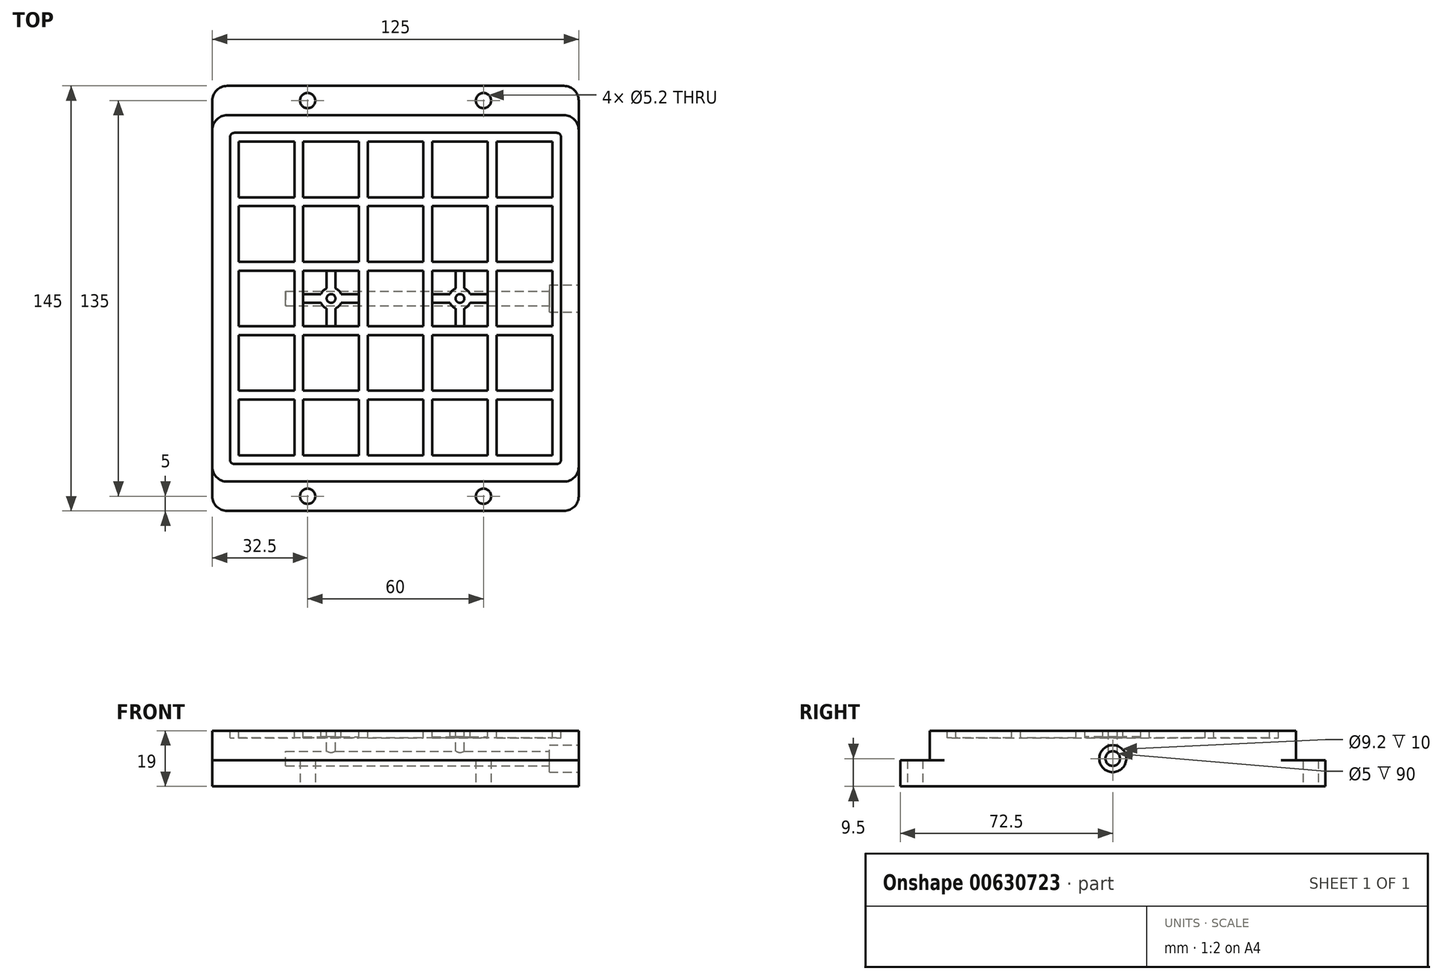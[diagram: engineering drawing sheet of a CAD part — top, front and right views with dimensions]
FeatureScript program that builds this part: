
annotation { "Feature Type Name" : "Feature", "Feature Type Description" : "" }
export const myFeature = defineFeature(function(context is Context, id is Id, definition is map)
    precondition{}
    {
        {
            var Q0;
            Q0=qCreatedBy(makeId("Top.planeOp"),FACE);
            var sketch = newSketch(context, id + "F0", { "sketchPlane" : qUnion([Q0])});
            skLineSegment(sketch, "E0.bottom", {"start": v(57.5, -72.5) * mm, "end": v(-57.5, -72.5) * mm});
            skLineSegment(sketch, "E0.top", {"start": v(57.5, 72.5) * mm, "end": v(-57.5, 72.5) * mm});
            skLineSegment(sketch, "E0.left", {"start": v(62.5, -67.5) * mm, "end": v(62.5, 67.5) * mm});
            skLineSegment(sketch, "E0.right", {"start": v(-62.5, -67.5) * mm, "end": v(-62.5, 67.5) * mm});
            skPoint(sketch, "E0.middle", {"position": v(0, 0) * mm});
            skPoint(sketch, "E1.visualSharp", {"position": v(-62.5, 72.5) * mm});
            skArc(sketch, "E1.filletArc", {"start": v(-57.5, 72.5) * mm, "mid": v(-61.04, 71.04) * mm, "end": v(-62.5, 67.5) * mm});
            skPoint(sketch, "E2.visualSharp", {"position": v(62.5, 72.5) * mm});
            skArc(sketch, "E2.filletArc", {"start": v(62.5, 67.5) * mm, "mid": v(61.04, 71.04) * mm, "end": v(57.5, 72.5) * mm});
            skPoint(sketch, "E3.visualSharp", {"position": v(62.5, -72.5) * mm});
            skArc(sketch, "E3.filletArc", {"start": v(57.5, -72.5) * mm, "mid": v(61.04, -71.04) * mm, "end": v(62.5, -67.5) * mm});
            skPoint(sketch, "E4.visualSharp", {"position": v(-62.5, -72.5) * mm});
            skArc(sketch, "E4.filletArc", {"start": v(-62.5, -67.5) * mm, "mid": v(-61.04, -71.04) * mm, "end": v(-57.5, -72.5) * mm});
            skLineSegment(sketch, "E5", {"start": v(-62.5, 67.5) * mm, "end": v(52.45, 67.5) * mm, "construction": true});
            skLineSegment(sketch, "E6", {"start": v(-48.85, -67.5) * mm, "end": v(50.9, -67.5) * mm, "construction": true});
            skCircle(sketch, "E7", {"center": v(-30, 67.5) * mm, "radius": 2.6 * mm});
            skCircle(sketch, "E8", {"center": v(30, 67.5) * mm, "radius": 2.6 * mm});
            skCircle(sketch, "E9", {"center": v(-30, -67.5) * mm, "radius": 2.6 * mm});
            skCircle(sketch, "E10", {"center": v(30, -67.5) * mm, "radius": 2.6 * mm});
            skSolve(sketch);
        }
        {
            var Q0;
            Q0=makeQuery(id+"F0.imprint","IMPRINT",FACE,{"disambiguationData":[TD([[makeQuery(id+"F0.imprint","IMPRINT",EDGE,{"derivedFrom":sQuery(id+"F0.wireOp",EDGE,"E0.bottom")}),-1.0]])]});
            extrude(context, id + "F1", {"entities" : qUnion([Q0]), "depth" : 9 * mm, "offsetDistance" : 25 * mm});
        }
        {
            var Q0;
            Q0=makeQuery(id+"F1.opExtrude","CAP_FACE",FACE,{"disambiguationData":[OSD([sQuery(id+"F0.wireOp",EDGE,"E0.bottom"),sQuery(id+"F0.wireOp",EDGE,"E0.top"),sQuery(id+"F0.wireOp",EDGE,"E0.left"),sQuery(id+"F0.wireOp",EDGE,"E0.right"),sQuery(id+"F0.wireOp",EDGE,"E1.filletArc"),sQuery(id+"F0.wireOp",EDGE,"E2.filletArc"),sQuery(id+"F0.wireOp",EDGE,"E3.filletArc"),sQuery(id+"F0.wireOp",EDGE,"E4.filletArc"),sQuery(id+"F0.wireOp",EDGE,"E7"),sQuery(id+"F0.wireOp",EDGE,"E8"),sQuery(id+"F0.wireOp",EDGE,"E9"),sQuery(id+"F0.wireOp",EDGE,"E10")])],"isStart":false});
            var sketch = newSketch(context, id + "F2", { "sketchPlane" : qUnion([Q0])});
            skLineSegment(sketch, "E11.bottom", {"start": v(57.5, -62.5) * mm, "end": v(-57.5, -62.5) * mm});
            skLineSegment(sketch, "E11.top", {"start": v(57.5, 62.5) * mm, "end": v(-57.5, 62.5) * mm});
            skLineSegment(sketch, "E11.left", {"start": v(62.5, -57.5) * mm, "end": v(62.5, 57.5) * mm});
            skLineSegment(sketch, "E11.right", {"start": v(-62.5, -57.5) * mm, "end": v(-62.5, 57.5) * mm});
            skPoint(sketch, "E11.middle", {"position": v(0, 0) * mm});
            skPoint(sketch, "E12.visualSharp", {"position": v(-62.5, 62.5) * mm});
            skArc(sketch, "E12.filletArc", {"start": v(-57.5, 62.5) * mm, "mid": v(-61.04, 61.04) * mm, "end": v(-62.5, 57.5) * mm});
            skPoint(sketch, "E13.visualSharp", {"position": v(62.5, 62.5) * mm});
            skArc(sketch, "E13.filletArc", {"start": v(62.5, 57.5) * mm, "mid": v(61.04, 61.04) * mm, "end": v(57.5, 62.5) * mm});
            skPoint(sketch, "E14.visualSharp", {"position": v(62.5, -62.5) * mm});
            skArc(sketch, "E14.filletArc", {"start": v(57.5, -62.5) * mm, "mid": v(61.04, -61.04) * mm, "end": v(62.5, -57.5) * mm});
            skPoint(sketch, "E15.visualSharp", {"position": v(-62.5, -62.5) * mm});
            skArc(sketch, "E15.filletArc", {"start": v(-62.5, -57.5) * mm, "mid": v(-61.04, -61.04) * mm, "end": v(-57.5, -62.5) * mm});
            skSolve(sketch);
        }
        {
            var Q0;
            Q0=makeQuery(id+"F2.imprint","IMPRINT",FACE,{"disambiguationData":[TD([[makeQuery(id+"F2.imprint","IMPRINT",EDGE,{"derivedFrom":sQuery(id+"F2.wireOp",EDGE,"E11.bottom")}),-1.0]])]});
            extrude(context, id + "F3", {"entities" : qUnion([Q0]), "operationType" : NewBodyOperationType.ADD, "depth" : 10 * mm, "offsetDistance" : 25 * mm});
        }
        {
            var Q0;
            Q0=makeQuery(id+"F3.boolean.opBoolean","MERGE",FACE,{"derivedFrom":[makeQuery(id+"F1.opExtrude","SWEPT_FACE",FACE,{"disambiguationData":[OSD([sQuery(id+"F0.wireOp",EDGE,"E0.left")])]}),makeQuery(id+"F3.opExtrude","SWEPT_FACE",FACE,{"disambiguationData":[OSD([sQuery(id+"F2.wireOp",EDGE,"E11.left")])]})]});
            var sketch = newSketch(context, id + "F4", { "sketchPlane" : qUnion([Q0])});
            skCircle(sketch, "E16", {"center": v(0, 9.5) * mm, "radius": 4.6 * mm});
            skCircle(sketch, "E17", {"center": v(0, 9.5) * mm, "radius": 2.5 * mm});
            skSolve(sketch);
        }
        {
            var Q0;
            Q0=makeQuery(id+"F4.imprint","IMPRINT",FACE,{"disambiguationData":[TD([[makeQuery(id+"F4.imprint","IMPRINT",EDGE,{"derivedFrom":sQuery(id+"F4.wireOp",EDGE,"E17")}),1.0]])]});
            extrude(context, id + "F5", {"entities" : qUnion([Q0]), "operationType" : NewBodyOperationType.REMOVE, "oppositeDirection" : true, "depth" : 100 * mm, "offsetDistance" : 25 * mm});
        }
        {
            var Q0;
            Q0=makeQuery(id+"F4.imprint","IMPRINT",FACE,{"disambiguationData":[TD([[makeQuery(id+"F4.imprint","IMPRINT",EDGE,{"derivedFrom":sQuery(id+"F4.wireOp",EDGE,"E16")}),1.0]])]});
            extrude(context, id + "F6", {"entities" : qUnion([Q0]), "operationType" : NewBodyOperationType.REMOVE, "oppositeDirection" : true, "depth" : 10 * mm, "offsetDistance" : 25 * mm});
        }
        {
            var Q0;
            Q0=makeQuery(id+"F3.opExtrude","CAP_FACE",FACE,{"disambiguationData":[OSD([sQuery(id+"F2.wireOp",EDGE,"E11.bottom"),sQuery(id+"F2.wireOp",EDGE,"E11.top"),sQuery(id+"F2.wireOp",EDGE,"E11.left"),sQuery(id+"F2.wireOp",EDGE,"E11.right"),sQuery(id+"F2.wireOp",EDGE,"E12.filletArc"),sQuery(id+"F2.wireOp",EDGE,"E13.filletArc"),sQuery(id+"F2.wireOp",EDGE,"E14.filletArc"),sQuery(id+"F2.wireOp",EDGE,"E15.filletArc")])],"isStart":false});
            var sketch = newSketch(context, id + "F7", { "sketchPlane" : qUnion([Q0])});
            skLineSegment(sketch, "E18.bottom", {"start": v(55, -55) * mm, "end": v(-55, -55) * mm, "construction": true});
            skLineSegment(sketch, "E18.top", {"start": v(55, 55) * mm, "end": v(-55, 55) * mm, "construction": true});
            skLineSegment(sketch, "E18.left", {"start": v(55, -55) * mm, "end": v(55, 55) * mm, "construction": true});
            skLineSegment(sketch, "E18.right", {"start": v(-55, -55) * mm, "end": v(-55, 55) * mm, "construction": true});
            skPoint(sketch, "E18.middle", {"position": v(0, 0) * mm});
            skLineSegment(sketch, "E19", {"start": v(-55, 33) * mm, "end": v(55, 33) * mm, "construction": true});
            skLineSegment(sketch, "E20", {"start": v(-55, 11) * mm, "end": v(55, 11) * mm, "construction": true});
            skLineSegment(sketch, "E21", {"start": v(-55, -11) * mm, "end": v(55, -11) * mm, "construction": true});
            skLineSegment(sketch, "E22", {"start": v(-55, -33) * mm, "end": v(55, -33) * mm, "construction": true});
            skLineSegment(sketch, "E23", {"start": v(-33, 55) * mm, "end": v(-33, -55) * mm, "construction": true});
            skLineSegment(sketch, "E24", {"start": v(-11, 55) * mm, "end": v(-11, -55) * mm, "construction": true});
            skLineSegment(sketch, "E25", {"start": v(11, 55) * mm, "end": v(11, -55) * mm, "construction": true});
            skLineSegment(sketch, "E26", {"start": v(33, 55) * mm, "end": v(33, -55) * mm, "construction": true});
            skArc(sketch, "E27.0.startCap", {"start": v(-55, 9.5) * mm, "mid": v(-56.5, 11) * mm, "end": v(-55, 12.5) * mm});
            skArc(sketch, "E27.0.endCap", {"start": v(55, 12.5) * mm, "mid": v(56.5, 11) * mm, "end": v(55, 9.5) * mm});
            skLineSegment(sketch, "E27.0.left", {"start": v(-55, 12.5) * mm, "end": v(55, 12.5) * mm});
            skLineSegment(sketch, "E27.0.right", {"start": v(-55, 9.5) * mm, "end": v(55, 9.5) * mm});
            skArc(sketch, "E28.0.startCap", {"start": v(-55, -12.5) * mm, "mid": v(-56.5, -11) * mm, "end": v(-55, -9.5) * mm});
            skArc(sketch, "E28.0.endCap", {"start": v(55, -9.5) * mm, "mid": v(56.5, -11) * mm, "end": v(55, -12.5) * mm});
            skLineSegment(sketch, "E28.0.left", {"start": v(-55, -9.5) * mm, "end": v(55, -9.5) * mm});
            skLineSegment(sketch, "E28.0.right", {"start": v(-55, -12.5) * mm, "end": v(55, -12.5) * mm});
            skArc(sketch, "E29.0.startCap", {"start": v(-55, -34.5) * mm, "mid": v(-56.5, -33) * mm, "end": v(-55, -31.5) * mm});
            skArc(sketch, "E29.0.endCap", {"start": v(55, -31.5) * mm, "mid": v(56.5, -33) * mm, "end": v(55, -34.5) * mm});
            skLineSegment(sketch, "E29.0.left", {"start": v(-55, -31.5) * mm, "end": v(55, -31.5) * mm});
            skLineSegment(sketch, "E29.0.right", {"start": v(-55, -34.5) * mm, "end": v(55, -34.5) * mm});
            skArc(sketch, "E30.0.startCap", {"start": v(55, -53.5) * mm, "mid": v(56.5, -55) * mm, "end": v(55, -56.5) * mm});
            skArc(sketch, "E30.0.endCap", {"start": v(-55, -56.5) * mm, "mid": v(-56.5, -55) * mm, "end": v(-55, -53.5) * mm});
            skLineSegment(sketch, "E30.0.left", {"start": v(55, -56.5) * mm, "end": v(-55, -56.5) * mm});
            skLineSegment(sketch, "E30.0.right", {"start": v(55, -53.5) * mm, "end": v(-55, -53.5) * mm});
            skArc(sketch, "E31.0.startCap", {"start": v(-55, 31.5) * mm, "mid": v(-56.5, 33) * mm, "end": v(-55, 34.5) * mm});
            skArc(sketch, "E31.0.endCap", {"start": v(55, 34.5) * mm, "mid": v(56.5, 33) * mm, "end": v(55, 31.5) * mm});
            skLineSegment(sketch, "E31.0.left", {"start": v(-55, 34.5) * mm, "end": v(55, 34.5) * mm});
            skLineSegment(sketch, "E31.0.right", {"start": v(-55, 31.5) * mm, "end": v(55, 31.5) * mm});
            skArc(sketch, "E32.0.startCap", {"start": v(55, 56.5) * mm, "mid": v(56.5, 55) * mm, "end": v(55, 53.5) * mm});
            skArc(sketch, "E32.0.endCap", {"start": v(-56.5, 55) * mm, "mid": v(-56.06, 56.06) * mm, "end": v(-55, 56.5) * mm});
            skLineSegment(sketch, "E32.0.left", {"start": v(55, 53.5) * mm, "end": v(-9.5, 53.5) * mm});
            skLineSegment(sketch, "E32.0.right", {"start": v(55, 56.5) * mm, "end": v(-55, 56.5) * mm});
            skArc(sketch, "E33.0.startCap", {"start": v(56.5, -55) * mm, "mid": v(55, -56.5) * mm, "end": v(53.5, -55) * mm});
            skArc(sketch, "E33.0.endCap", {"start": v(53.5, 55) * mm, "mid": v(55, 56.5) * mm, "end": v(56.5, 55) * mm});
            skLineSegment(sketch, "E33.0.left", {"start": v(53.5, -55) * mm, "end": v(53.5, 55) * mm});
            skLineSegment(sketch, "E33.0.right", {"start": v(56.5, -55) * mm, "end": v(56.5, 55) * mm});
            skArc(sketch, "E34.0.startCap", {"start": v(31.5, 55) * mm, "mid": v(33, 56.5) * mm, "end": v(34.5, 55) * mm});
            skArc(sketch, "E34.0.endCap", {"start": v(34.5, -55) * mm, "mid": v(33, -56.5) * mm, "end": v(31.5, -55) * mm});
            skLineSegment(sketch, "E34.0.left", {"start": v(34.5, 55) * mm, "end": v(34.5, -55) * mm});
            skLineSegment(sketch, "E34.0.right", {"start": v(31.5, 55) * mm, "end": v(31.5, -55) * mm});
            skArc(sketch, "E35.0.endCap", {"start": v(-9.5, -55) * mm, "mid": v(-11, -56.5) * mm, "end": v(-12.5, -55) * mm});
            skLineSegment(sketch, "E35.0.left", {"start": v(-9.5, 53.5) * mm, "end": v(-9.5, -55) * mm});
            skLineSegment(sketch, "E35.0.right", {"start": v(-12.5, 53.5) * mm, "end": v(-12.5, -55) * mm});
            skArc(sketch, "E36.0.endCap", {"start": v(-31.5, -55) * mm, "mid": v(-33, -56.5) * mm, "end": v(-34.5, -55) * mm});
            skLineSegment(sketch, "E36.0.left", {"start": v(-31.5, 53.5) * mm, "end": v(-31.5, -55) * mm});
            skLineSegment(sketch, "E36.0.right", {"start": v(-34.5, 53.5) * mm, "end": v(-34.5, -55) * mm});
            skArc(sketch, "E37.0.startCap", {"start": v(9.5, 55) * mm, "mid": v(11, 56.5) * mm, "end": v(12.5, 55) * mm});
            skArc(sketch, "E37.0.endCap", {"start": v(12.5, -55) * mm, "mid": v(11, -56.5) * mm, "end": v(9.5, -55) * mm});
            skLineSegment(sketch, "E37.0.left", {"start": v(12.5, 55) * mm, "end": v(12.5, -55) * mm});
            skLineSegment(sketch, "E37.0.right", {"start": v(9.5, 55) * mm, "end": v(9.5, -55) * mm});
            skArc(sketch, "E38.0.startCap", {"start": v(-53.5, -55) * mm, "mid": v(-55, -56.5) * mm, "end": v(-56.5, -55) * mm});
            skLineSegment(sketch, "E38.0.left", {"start": v(-56.5, -55) * mm, "end": v(-56.5, 55) * mm});
            skLineSegment(sketch, "E38.0.right", {"start": v(-53.5, -55) * mm, "end": v(-53.5, 53.5) * mm});
            skLineSegment(sketch, "E39.trimOffspring", {"start": v(-34.5, 53.5) * mm, "end": v(-53.5, 53.5) * mm});
            skLineSegment(sketch, "E40.trimOffspring", {"start": v(-12.5, 53.5) * mm, "end": v(-31.5, 53.5) * mm});
            skSolve(sketch);
        }
        {
            var Q0;
            {var subQ1=sQuery(id+"F7.wireOp",EDGE,"E32.0.endCap");Q0=makeQuery(id+"F7.imprint","IMPRINT",FACE,{"disambiguationData":[TD([[makeQuery(id+"F7.imprint","IMPRINT",EDGE,{"derivedFrom":subQ1}),1.0]])]});}
            var sketch = newSketch(context, id + "F8", { "sketchPlane" : qUnion([Q0])});
            skLineSegment(sketch, "E41.bottom", {"start": v(-53.5, 53.5) * mm, "end": v(-34.5, 53.5) * mm});
            skLineSegment(sketch, "E41.top", {"start": v(-53.5, 34.5) * mm, "end": v(-34.5, 34.5) * mm});
            skLineSegment(sketch, "E41.left", {"start": v(-53.5, 53.5) * mm, "end": v(-53.5, 34.5) * mm});
            skLineSegment(sketch, "E41.right", {"start": v(-34.5, 53.5) * mm, "end": v(-34.5, 34.5) * mm});
            skLineSegment(sketch, "E42.0.1.0", {"start": v(-53.5, 31.5) * mm, "end": v(-34.5, 31.5) * mm});
            skLineSegment(sketch, "E42.0.1.1", {"start": v(-34.5, 31.5) * mm, "end": v(-34.5, 12.5) * mm});
            skLineSegment(sketch, "E42.0.1.2", {"start": v(-53.5, 12.5) * mm, "end": v(-34.5, 12.5) * mm});
            skLineSegment(sketch, "E42.0.1.3", {"start": v(-53.5, 31.5) * mm, "end": v(-53.5, 12.5) * mm});
            skLineSegment(sketch, "E42.0.2.0", {"start": v(-53.5, 9.5) * mm, "end": v(-34.5, 9.5) * mm});
            skLineSegment(sketch, "E42.0.2.1", {"start": v(-34.5, 9.5) * mm, "end": v(-34.5, -9.5) * mm});
            skLineSegment(sketch, "E42.0.2.2", {"start": v(-53.5, -9.5) * mm, "end": v(-34.5, -9.5) * mm});
            skLineSegment(sketch, "E42.0.2.3", {"start": v(-53.5, 9.5) * mm, "end": v(-53.5, -9.5) * mm});
            skLineSegment(sketch, "E42.0.3.0", {"start": v(-53.5, -12.5) * mm, "end": v(-34.5, -12.5) * mm});
            skLineSegment(sketch, "E42.0.3.1", {"start": v(-34.5, -12.5) * mm, "end": v(-34.5, -31.5) * mm});
            skLineSegment(sketch, "E42.0.3.2", {"start": v(-53.5, -31.5) * mm, "end": v(-34.5, -31.5) * mm});
            skLineSegment(sketch, "E42.0.3.3", {"start": v(-53.5, -12.5) * mm, "end": v(-53.5, -31.5) * mm});
            skLineSegment(sketch, "E42.0.4.0", {"start": v(-53.5, -34.5) * mm, "end": v(-34.5, -34.5) * mm});
            skLineSegment(sketch, "E42.0.4.1", {"start": v(-34.5, -34.5) * mm, "end": v(-34.5, -53.5) * mm});
            skLineSegment(sketch, "E42.0.4.2", {"start": v(-53.5, -53.5) * mm, "end": v(-34.5, -53.5) * mm});
            skLineSegment(sketch, "E42.0.4.3", {"start": v(-53.5, -34.5) * mm, "end": v(-53.5, -53.5) * mm});
            skLineSegment(sketch, "E42.1.0.0", {"start": v(-31.5, 53.5) * mm, "end": v(-12.5, 53.5) * mm});
            skLineSegment(sketch, "E42.1.0.1", {"start": v(-12.5, 53.5) * mm, "end": v(-12.5, 34.5) * mm});
            skLineSegment(sketch, "E42.1.0.2", {"start": v(-31.5, 34.5) * mm, "end": v(-12.5, 34.5) * mm});
            skLineSegment(sketch, "E42.1.0.3", {"start": v(-31.5, 53.5) * mm, "end": v(-31.5, 34.5) * mm});
            skLineSegment(sketch, "E42.1.1.0", {"start": v(-31.5, 31.5) * mm, "end": v(-12.5, 31.5) * mm});
            skLineSegment(sketch, "E42.1.1.1", {"start": v(-12.5, 31.5) * mm, "end": v(-12.5, 12.5) * mm});
            skLineSegment(sketch, "E42.1.1.2", {"start": v(-31.5, 12.5) * mm, "end": v(-12.5, 12.5) * mm});
            skLineSegment(sketch, "E42.1.1.3", {"start": v(-31.5, 31.5) * mm, "end": v(-31.5, 12.5) * mm});
            skLineSegment(sketch, "E42.1.2.0", {"start": v(-31.5, 9.5) * mm, "end": v(-12.5, 9.5) * mm});
            skLineSegment(sketch, "E42.1.2.1", {"start": v(-12.5, 9.5) * mm, "end": v(-12.5, -9.5) * mm});
            skLineSegment(sketch, "E42.1.2.2", {"start": v(-31.5, -9.5) * mm, "end": v(-12.5, -9.5) * mm});
            skLineSegment(sketch, "E42.1.2.3", {"start": v(-31.5, 9.5) * mm, "end": v(-31.5, -9.5) * mm});
            skLineSegment(sketch, "E42.1.3.0", {"start": v(-31.5, -12.5) * mm, "end": v(-12.5, -12.5) * mm});
            skLineSegment(sketch, "E42.1.3.1", {"start": v(-12.5, -12.5) * mm, "end": v(-12.5, -31.5) * mm});
            skLineSegment(sketch, "E42.1.3.2", {"start": v(-31.5, -31.5) * mm, "end": v(-12.5, -31.5) * mm});
            skLineSegment(sketch, "E42.1.3.3", {"start": v(-31.5, -12.5) * mm, "end": v(-31.5, -31.5) * mm});
            skLineSegment(sketch, "E42.1.4.0", {"start": v(-31.5, -34.5) * mm, "end": v(-12.5, -34.5) * mm});
            skLineSegment(sketch, "E42.1.4.1", {"start": v(-12.5, -34.5) * mm, "end": v(-12.5, -53.5) * mm});
            skLineSegment(sketch, "E42.1.4.2", {"start": v(-31.5, -53.5) * mm, "end": v(-12.5, -53.5) * mm});
            skLineSegment(sketch, "E42.1.4.3", {"start": v(-31.5, -34.5) * mm, "end": v(-31.5, -53.5) * mm});
            skLineSegment(sketch, "E42.2.0.0", {"start": v(-9.5, 53.5) * mm, "end": v(9.5, 53.5) * mm});
            skLineSegment(sketch, "E42.2.0.1", {"start": v(9.5, 53.5) * mm, "end": v(9.5, 34.5) * mm});
            skLineSegment(sketch, "E42.2.0.2", {"start": v(-9.5, 34.5) * mm, "end": v(9.5, 34.5) * mm});
            skLineSegment(sketch, "E42.2.0.3", {"start": v(-9.5, 53.5) * mm, "end": v(-9.5, 34.5) * mm});
            skLineSegment(sketch, "E42.2.1.0", {"start": v(-9.5, 31.5) * mm, "end": v(9.5, 31.5) * mm});
            skLineSegment(sketch, "E42.2.1.1", {"start": v(9.5, 31.5) * mm, "end": v(9.5, 12.5) * mm});
            skLineSegment(sketch, "E42.2.1.2", {"start": v(-9.5, 12.5) * mm, "end": v(9.5, 12.5) * mm});
            skLineSegment(sketch, "E42.2.1.3", {"start": v(-9.5, 31.5) * mm, "end": v(-9.5, 12.5) * mm});
            skLineSegment(sketch, "E42.2.2.0", {"start": v(-9.5, 9.5) * mm, "end": v(9.5, 9.5) * mm});
            skLineSegment(sketch, "E42.2.2.1", {"start": v(9.5, 9.5) * mm, "end": v(9.5, -9.5) * mm});
            skLineSegment(sketch, "E42.2.2.2", {"start": v(-9.5, -9.5) * mm, "end": v(9.5, -9.5) * mm});
            skLineSegment(sketch, "E42.2.2.3", {"start": v(-9.5, 9.5) * mm, "end": v(-9.5, -9.5) * mm});
            skLineSegment(sketch, "E42.2.3.0", {"start": v(-9.5, -12.5) * mm, "end": v(9.5, -12.5) * mm});
            skLineSegment(sketch, "E42.2.3.1", {"start": v(9.5, -12.5) * mm, "end": v(9.5, -31.5) * mm});
            skLineSegment(sketch, "E42.2.3.2", {"start": v(-9.5, -31.5) * mm, "end": v(9.5, -31.5) * mm});
            skLineSegment(sketch, "E42.2.3.3", {"start": v(-9.5, -12.5) * mm, "end": v(-9.5, -31.5) * mm});
            skLineSegment(sketch, "E42.2.4.0", {"start": v(-9.5, -34.5) * mm, "end": v(9.5, -34.5) * mm});
            skLineSegment(sketch, "E42.2.4.1", {"start": v(9.5, -34.5) * mm, "end": v(9.5, -53.5) * mm});
            skLineSegment(sketch, "E42.2.4.2", {"start": v(-9.5, -53.5) * mm, "end": v(9.5, -53.5) * mm});
            skLineSegment(sketch, "E42.2.4.3", {"start": v(-9.5, -34.5) * mm, "end": v(-9.5, -53.5) * mm});
            skLineSegment(sketch, "E42.3.0.0", {"start": v(12.5, 53.5) * mm, "end": v(31.5, 53.5) * mm});
            skLineSegment(sketch, "E42.3.0.1", {"start": v(31.5, 53.5) * mm, "end": v(31.5, 34.5) * mm});
            skLineSegment(sketch, "E42.3.0.2", {"start": v(12.5, 34.5) * mm, "end": v(31.5, 34.5) * mm});
            skLineSegment(sketch, "E42.3.0.3", {"start": v(12.5, 53.5) * mm, "end": v(12.5, 34.5) * mm});
            skLineSegment(sketch, "E42.3.1.0", {"start": v(12.5, 31.5) * mm, "end": v(31.5, 31.5) * mm});
            skLineSegment(sketch, "E42.3.1.1", {"start": v(31.5, 31.5) * mm, "end": v(31.5, 12.5) * mm});
            skLineSegment(sketch, "E42.3.1.2", {"start": v(12.5, 12.5) * mm, "end": v(31.5, 12.5) * mm});
            skLineSegment(sketch, "E42.3.1.3", {"start": v(12.5, 31.5) * mm, "end": v(12.5, 12.5) * mm});
            skLineSegment(sketch, "E42.3.2.0", {"start": v(12.5, 9.5) * mm, "end": v(31.5, 9.5) * mm});
            skLineSegment(sketch, "E42.3.2.1", {"start": v(31.5, 9.5) * mm, "end": v(31.5, -9.5) * mm});
            skLineSegment(sketch, "E42.3.2.2", {"start": v(12.5, -9.5) * mm, "end": v(31.5, -9.5) * mm});
            skLineSegment(sketch, "E42.3.2.3", {"start": v(12.5, 9.5) * mm, "end": v(12.5, -9.5) * mm});
            skLineSegment(sketch, "E42.3.3.0", {"start": v(12.5, -12.5) * mm, "end": v(31.5, -12.5) * mm});
            skLineSegment(sketch, "E42.3.3.1", {"start": v(31.5, -12.5) * mm, "end": v(31.5, -31.5) * mm});
            skLineSegment(sketch, "E42.3.3.2", {"start": v(12.5, -31.5) * mm, "end": v(31.5, -31.5) * mm});
            skLineSegment(sketch, "E42.3.3.3", {"start": v(12.5, -12.5) * mm, "end": v(12.5, -31.5) * mm});
            skLineSegment(sketch, "E42.3.4.0", {"start": v(12.5, -34.5) * mm, "end": v(31.5, -34.5) * mm});
            skLineSegment(sketch, "E42.3.4.1", {"start": v(31.5, -34.5) * mm, "end": v(31.5, -53.5) * mm});
            skLineSegment(sketch, "E42.3.4.2", {"start": v(12.5, -53.5) * mm, "end": v(31.5, -53.5) * mm});
            skLineSegment(sketch, "E42.3.4.3", {"start": v(12.5, -34.5) * mm, "end": v(12.5, -53.5) * mm});
            skLineSegment(sketch, "E42.4.0.0", {"start": v(34.5, 53.5) * mm, "end": v(53.5, 53.5) * mm});
            skLineSegment(sketch, "E42.4.0.1", {"start": v(53.5, 53.5) * mm, "end": v(53.5, 34.5) * mm});
            skLineSegment(sketch, "E42.4.0.2", {"start": v(34.5, 34.5) * mm, "end": v(53.5, 34.5) * mm});
            skLineSegment(sketch, "E42.4.0.3", {"start": v(34.5, 53.5) * mm, "end": v(34.5, 34.5) * mm});
            skLineSegment(sketch, "E42.4.1.0", {"start": v(34.5, 31.5) * mm, "end": v(53.5, 31.5) * mm});
            skLineSegment(sketch, "E42.4.1.1", {"start": v(53.5, 31.5) * mm, "end": v(53.5, 12.5) * mm});
            skLineSegment(sketch, "E42.4.1.2", {"start": v(34.5, 12.5) * mm, "end": v(53.5, 12.5) * mm});
            skLineSegment(sketch, "E42.4.1.3", {"start": v(34.5, 31.5) * mm, "end": v(34.5, 12.5) * mm});
            skLineSegment(sketch, "E42.4.2.0", {"start": v(34.5, 9.5) * mm, "end": v(53.5, 9.5) * mm});
            skLineSegment(sketch, "E42.4.2.1", {"start": v(53.5, 9.5) * mm, "end": v(53.5, -9.5) * mm});
            skLineSegment(sketch, "E42.4.2.2", {"start": v(34.5, -9.5) * mm, "end": v(53.5, -9.5) * mm});
            skLineSegment(sketch, "E42.4.2.3", {"start": v(34.5, 9.5) * mm, "end": v(34.5, -9.5) * mm});
            skLineSegment(sketch, "E42.4.3.0", {"start": v(34.5, -12.5) * mm, "end": v(53.5, -12.5) * mm});
            skLineSegment(sketch, "E42.4.3.1", {"start": v(53.5, -12.5) * mm, "end": v(53.5, -31.5) * mm});
            skLineSegment(sketch, "E42.4.3.2", {"start": v(34.5, -31.5) * mm, "end": v(53.5, -31.5) * mm});
            skLineSegment(sketch, "E42.4.3.3", {"start": v(34.5, -12.5) * mm, "end": v(34.5, -31.5) * mm});
            skLineSegment(sketch, "E42.4.4.0", {"start": v(34.5, -34.5) * mm, "end": v(53.5, -34.5) * mm});
            skLineSegment(sketch, "E42.4.4.1", {"start": v(53.5, -34.5) * mm, "end": v(53.5, -53.5) * mm});
            skLineSegment(sketch, "E42.4.4.2", {"start": v(34.5, -53.5) * mm, "end": v(53.5, -53.5) * mm});
            skLineSegment(sketch, "E42.4.4.3", {"start": v(34.5, -34.5) * mm, "end": v(34.5, -53.5) * mm});
            skLineSegment(sketch, "E42.direction1", {"start": v(-53.5, 34.5) * mm, "end": v(-31.5, 34.5) * mm, "construction": true});
            skLineSegment(sketch, "E42.direction2", {"start": v(-53.5, 34.5) * mm, "end": v(-53.5, 12.5) * mm, "construction": true});
            skLineSegment(sketch, "E43.bottom", {"start": v(55, -56.5) * mm, "end": v(-55, -56.5) * mm});
            skLineSegment(sketch, "E43.top", {"start": v(55, 56.5) * mm, "end": v(-55, 56.5) * mm});
            skLineSegment(sketch, "E43.left", {"start": v(56.5, -55) * mm, "end": v(56.5, 55) * mm});
            skLineSegment(sketch, "E43.right", {"start": v(-56.5, -55) * mm, "end": v(-56.5, 55) * mm});
            skPoint(sketch, "E43.middle", {"position": v(0, 0) * mm});
            skPoint(sketch, "E44.visualSharp", {"position": v(-56.5, -56.5) * mm});
            skArc(sketch, "E44.filletArc", {"start": v(-56.5, -55) * mm, "mid": v(-56.06, -56.06) * mm, "end": v(-55, -56.5) * mm});
            skPoint(sketch, "E45.visualSharp", {"position": v(56.5, -56.5) * mm});
            skArc(sketch, "E45.filletArc", {"start": v(55, -56.5) * mm, "mid": v(56.06, -56.06) * mm, "end": v(56.5, -55) * mm});
            skPoint(sketch, "E46.visualSharp", {"position": v(56.5, 56.5) * mm});
            skArc(sketch, "E46.filletArc", {"start": v(56.5, 55) * mm, "mid": v(56.06, 56.06) * mm, "end": v(55, 56.5) * mm});
            skPoint(sketch, "E47.visualSharp", {"position": v(-56.5, 56.5) * mm});
            skArc(sketch, "E47.filletArc", {"start": v(-55, 56.5) * mm, "mid": v(-56.06, 56.06) * mm, "end": v(-56.5, 55) * mm});
            skSolve(sketch);
        }
        {
            var Q0;
            Q0=qSketchRegion(id+"F8",true);
            extrude(context, id + "F9", {"entities" : qUnion([Q0]), "operationType" : NewBodyOperationType.REMOVE, "oppositeDirection" : true, "depth" : 2.5 * mm, "offsetDistance" : 25 * mm});
        }
        {
            var Q0;
            Q0=makeQuery(id+"F9.boolean.opBoolean","SPLIT",FACE,{"disambiguationData":[TD([makeQuery(id+"F9.opExtrude","SWEPT_FACE",FACE,{"disambiguationData":[OSD([sQuery(id+"F8.wireOp",EDGE,"E42.1.2.0")])]})])],"derivedFrom":makeQuery(id+"F3.opExtrude","CAP_FACE",FACE,{"disambiguationData":[OSD([sQuery(id+"F2.wireOp",EDGE,"E11.bottom"),sQuery(id+"F2.wireOp",EDGE,"E11.top"),sQuery(id+"F2.wireOp",EDGE,"E11.left"),sQuery(id+"F2.wireOp",EDGE,"E11.right"),sQuery(id+"F2.wireOp",EDGE,"E12.filletArc"),sQuery(id+"F2.wireOp",EDGE,"E13.filletArc"),sQuery(id+"F2.wireOp",EDGE,"E14.filletArc"),sQuery(id+"F2.wireOp",EDGE,"E15.filletArc")])],"isStart":false})});
            var sketch = newSketch(context, id + "F10", { "sketchPlane" : qUnion([Q0])});
            skCircle(sketch, "E48", {"center": v(-22, 0) * mm, "radius": 1.5 * mm});
            skCircle(sketch, "E49", {"center": v(22, 0) * mm, "radius": 1.5 * mm});
            skSolve(sketch);
        }
        {
            var Q0;
            Q0=qSketchRegion(id+"F10",true);
            extrude(context, id + "F11", {"entities" : qUnion([Q0]), "operationType" : NewBodyOperationType.REMOVE, "oppositeDirection" : true, "depth" : 10 * mm, "offsetDistance" : 25 * mm});
        }
        {
            var Q0;
            Q0=makeQuery(id+"F9.boolean.opBoolean","SPLIT",FACE,{"disambiguationData":[TD([makeQuery(id+"F9.opExtrude","SWEPT_FACE",FACE,{"disambiguationData":[OSD([sQuery(id+"F8.wireOp",EDGE,"E42.1.2.0")])]})])],"derivedFrom":makeQuery(id+"F3.opExtrude","CAP_FACE",FACE,{"disambiguationData":[OSD([sQuery(id+"F2.wireOp",EDGE,"E11.bottom"),sQuery(id+"F2.wireOp",EDGE,"E11.top"),sQuery(id+"F2.wireOp",EDGE,"E11.left"),sQuery(id+"F2.wireOp",EDGE,"E11.right"),sQuery(id+"F2.wireOp",EDGE,"E12.filletArc"),sQuery(id+"F2.wireOp",EDGE,"E13.filletArc"),sQuery(id+"F2.wireOp",EDGE,"E14.filletArc"),sQuery(id+"F2.wireOp",EDGE,"E15.filletArc")])],"isStart":false})});
            var sketch = newSketch(context, id + "F12", { "sketchPlane" : qUnion([Q0])});
            skLineSegment(sketch, "E50", {"start": v(-31.5, 0) * mm, "end": v(-12.5, 0) * mm, "construction": true});
            skLineSegment(sketch, "E51", {"start": v(12.5, 0) * mm, "end": v(31.5, 0) * mm, "construction": true});
            skLineSegment(sketch, "E52", {"start": v(22, 9.5) * mm, "end": v(22, -9.5) * mm, "construction": true});
            skLineSegment(sketch, "E53", {"start": v(-22, 9.5) * mm, "end": v(-22, -9.5) * mm, "construction": true});
            skArc(sketch, "E54.0.startCap", {"start": v(12.5, -1.5) * mm, "mid": v(11, 0) * mm, "end": v(12.5, 1.5) * mm});
            skArc(sketch, "E54.0.endCap", {"start": v(31.5, 1.5) * mm, "mid": v(33, 0) * mm, "end": v(31.5, -1.5) * mm});
            skLineSegment(sketch, "E54.0.left", {"start": v(12.5, 1.5) * mm, "end": v(20.5, 1.5) * mm});
            skLineSegment(sketch, "E54.0.right", {"start": v(12.5, -1.5) * mm, "end": v(20.5, -1.5) * mm});
            skArc(sketch, "E54.1.startCap", {"start": v(20.5, 9.5) * mm, "mid": v(22, 11) * mm, "end": v(23.5, 9.5) * mm});
            skArc(sketch, "E54.1.endCap", {"start": v(23.5, -9.5) * mm, "mid": v(22, -11) * mm, "end": v(20.5, -9.5) * mm});
            skLineSegment(sketch, "E54.1.left", {"start": v(23.5, 9.5) * mm, "end": v(23.5, 1.5) * mm});
            skLineSegment(sketch, "E54.1.right", {"start": v(20.5, 9.5) * mm, "end": v(20.5, 1.5) * mm});
            skArc(sketch, "E54.2.startCap", {"start": v(-31.5, -1.5) * mm, "mid": v(-33, 0) * mm, "end": v(-31.5, 1.5) * mm});
            skArc(sketch, "E54.2.endCap", {"start": v(-12.5, 1.5) * mm, "mid": v(-11, 0) * mm, "end": v(-12.5, -1.5) * mm});
            skLineSegment(sketch, "E54.2.left", {"start": v(-31.5, 1.5) * mm, "end": v(-23.5, 1.5) * mm});
            skLineSegment(sketch, "E54.2.right", {"start": v(-31.5, -1.5) * mm, "end": v(-23.5, -1.5) * mm});
            skArc(sketch, "E54.3.startCap", {"start": v(-23.5, 9.5) * mm, "mid": v(-22, 11) * mm, "end": v(-20.5, 9.5) * mm});
            skArc(sketch, "E54.3.endCap", {"start": v(-20.5, -9.5) * mm, "mid": v(-22, -11) * mm, "end": v(-23.5, -9.5) * mm});
            skLineSegment(sketch, "E54.3.left", {"start": v(-20.5, 9.5) * mm, "end": v(-20.5, 1.5) * mm});
            skLineSegment(sketch, "E54.3.right", {"start": v(-23.5, 9.5) * mm, "end": v(-23.5, 1.5) * mm});
            skLineSegment(sketch, "E55.trimOffspring", {"start": v(-20.5, 1.5) * mm, "end": v(-12.5, 1.5) * mm});
            skLineSegment(sketch, "E56.trimOffspring", {"start": v(-23.5, -1.5) * mm, "end": v(-23.5, -9.5) * mm});
            skLineSegment(sketch, "E57.trimOffspring", {"start": v(-20.5, -1.5) * mm, "end": v(-12.5, -1.5) * mm});
            skLineSegment(sketch, "E58.trimOffspring", {"start": v(-20.5, -1.5) * mm, "end": v(-20.5, -9.5) * mm});
            skLineSegment(sketch, "E59.trimOffspring", {"start": v(23.5, 1.5) * mm, "end": v(31.5, 1.5) * mm});
            skLineSegment(sketch, "E60.trimOffspring", {"start": v(20.5, -1.5) * mm, "end": v(20.5, -9.5) * mm});
            skLineSegment(sketch, "E61.trimOffspring", {"start": v(23.5, -1.5) * mm, "end": v(31.5, -1.5) * mm});
            skLineSegment(sketch, "E62.trimOffspring", {"start": v(23.5, -1.5) * mm, "end": v(23.5, -9.5) * mm});
            skSolve(sketch);
        }
        {
            var Q0;
            Q0=qSketchRegion(id+"F12",true);
            extrude(context, id + "F13", {"entities" : qUnion([Q0]), "operationType" : NewBodyOperationType.REMOVE, "oppositeDirection" : true, "depth" : 2 * mm, "offsetDistance" : 25 * mm});
        }
        {
            var Q0;
            {var subQ0=makeQuery(id+"F9.opExtrude","SWEPT_FACE",FACE,{"disambiguationData":[OSD([sQuery(id+"F8.wireOp",EDGE,"E42.1.2.0")])]});Q0=makeQuery(id+"F13.boolean.opBoolean","SPLIT",FACE,{"disambiguationData":[TD([makeQuery(id+"F13.opExtrude","SWEPT_FACE",FACE,{"disambiguationData":[OSD([sQuery(id+"F12.wireOp",EDGE,"E54.3.left")])]})])],"derivedFrom":makeQuery(id+"F9.boolean.opBoolean","SPLIT",FACE,{"disambiguationData":[TD([subQ0])],"derivedFrom":makeQuery(id+"F3.opExtrude","CAP_FACE",FACE,{"disambiguationData":[OSD([sQuery(id+"F2.wireOp",EDGE,"E11.bottom"),sQuery(id+"F2.wireOp",EDGE,"E11.top"),sQuery(id+"F2.wireOp",EDGE,"E11.left"),sQuery(id+"F2.wireOp",EDGE,"E11.right"),sQuery(id+"F2.wireOp",EDGE,"E12.filletArc"),sQuery(id+"F2.wireOp",EDGE,"E13.filletArc"),sQuery(id+"F2.wireOp",EDGE,"E14.filletArc"),sQuery(id+"F2.wireOp",EDGE,"E15.filletArc")])],"isStart":false})})});}
            var sketch = newSketch(context, id + "F14", { "sketchPlane" : qUnion([Q0])});
            skCircle(sketch, "E63", {"center": v(-22, 0) * mm, "radius": 3.75 * mm});
            skCircle(sketch, "E64", {"center": v(22, 0) * mm, "radius": 3.75 * mm});
            skSolve(sketch);
        }
        {
            var Q0;
            Q0=qSketchRegion(id+"F14",true);
            extrude(context, id + "F15", {"entities" : qUnion([Q0]), "operationType" : NewBodyOperationType.REMOVE, "oppositeDirection" : true, "depth" : 2 * mm, "offsetDistance" : 25 * mm});
        }
    });
